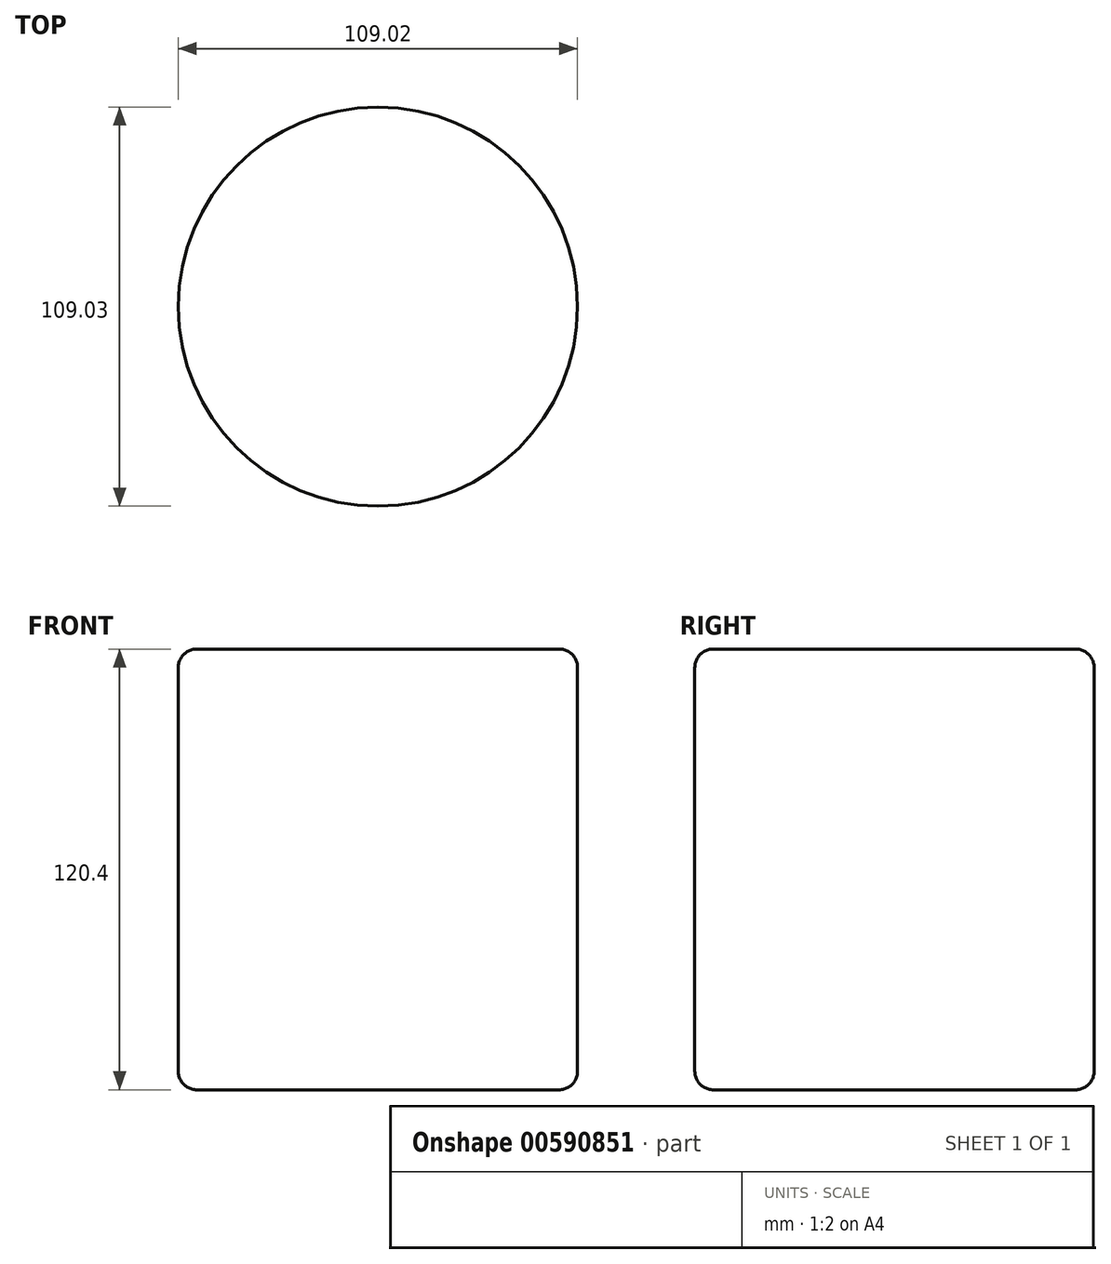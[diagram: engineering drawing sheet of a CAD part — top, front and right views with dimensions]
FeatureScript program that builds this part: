
annotation { "Feature Type Name" : "Feature", "Feature Type Description" : "" }
export const myFeature = defineFeature(function(context is Context, id is Id, definition is map)
    precondition{}
    {
        {
            var Q0;
            Q0=qCreatedBy(makeId("Top.planeOp"),FACE);
            var sketch = newSketch(context, id + "F0", { "sketchPlane" : qUnion([Q0])});
            skCircle(sketch, "E0", {"center": v(-4.82, 10.07) * mm, "radius": 54.51 * mm});
            skSolve(sketch);
        }
        {
            var Q0;
            Q0 = qSketchRegion(id + "F0", true);
            var Q1;
            Q1=makeQuery(id+"F0.imprint","IMPRINT",FACE,{"disambiguationData":[TD([[makeQuery(id+"F0.imprint","IMPRINT",EDGE,{"derivedFrom":sQuery(id+"F0.wireOp",EDGE,"E0")}),1.0]])]});
            extrude(context, id + "F1", {"entities" : qUnion([Q0, Q1]), "depth" : 120.4 * mm, "offsetDistance" : 25.4 * mm});
        }
        {
            var Q0;
            Q0=makeQuery(id+"F1.opExtrude","CAP_EDGE",EDGE,{"disambiguationData":[OSD([sQuery(id+"F0.wireOp",EDGE,"E0")])],"isStart":false});
            var Q1;
            Q1=makeQuery(id+"F1.opExtrude","CAP_EDGE",EDGE,{"disambiguationData":[OSD([sQuery(id+"F0.wireOp",EDGE,"E0")])],"isStart":true});
            fillet(context, id + "F2", {"entities" : qUnion([Q0, Q1]), "radius" : 5.08 * mm, "tangentPropagation" : true, "allowEdgeOverflow" : false});
        }
    });
